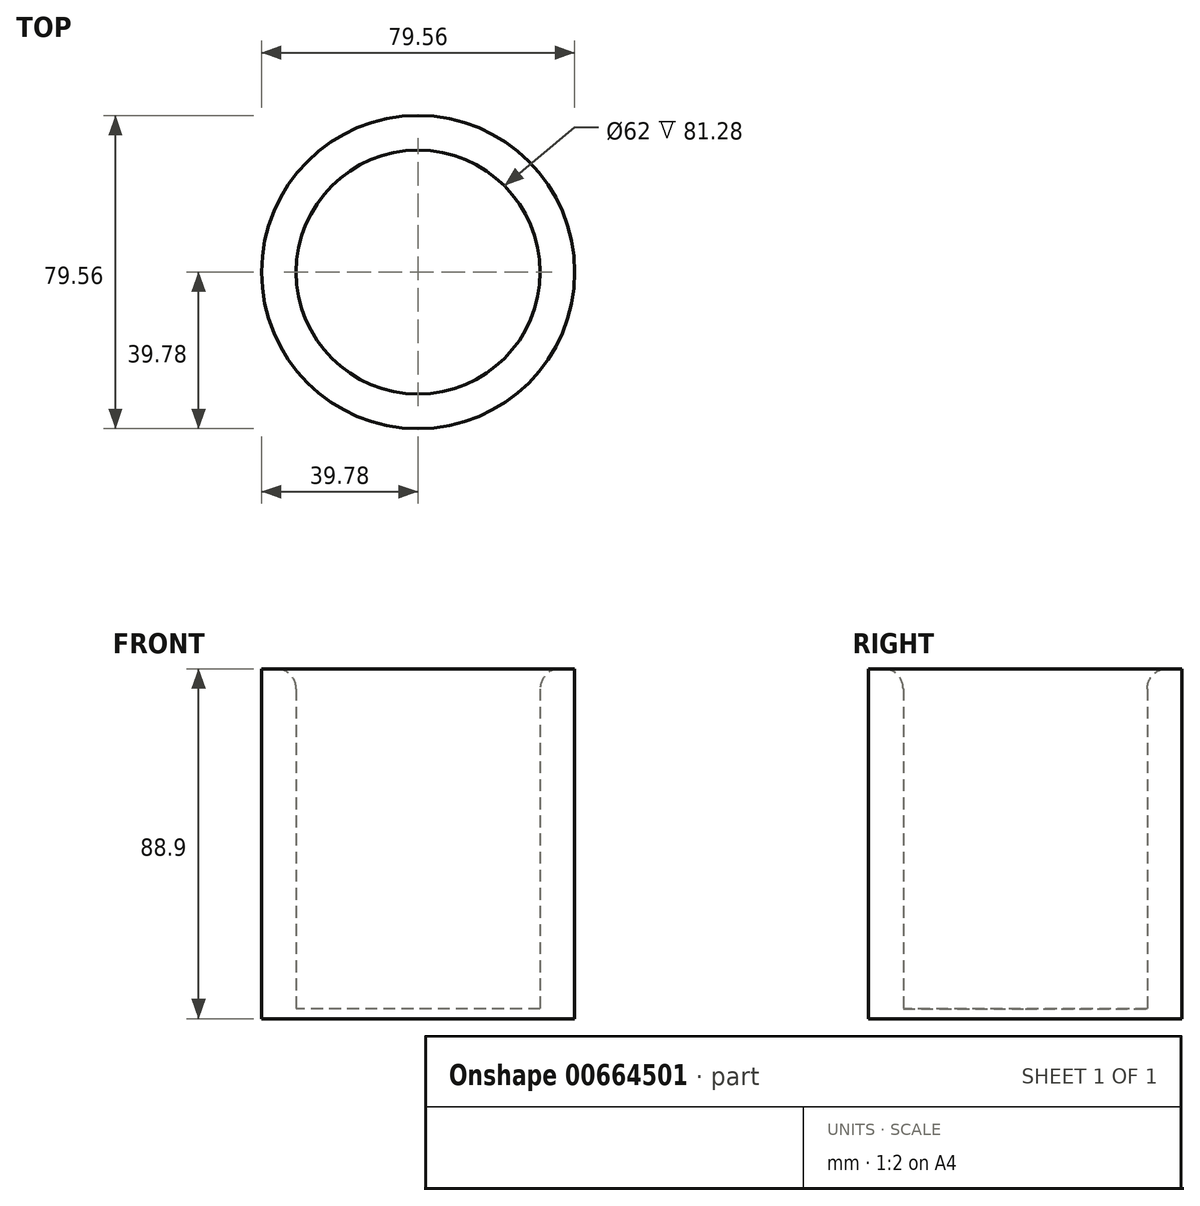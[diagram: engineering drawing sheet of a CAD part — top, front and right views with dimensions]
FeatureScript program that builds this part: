
annotation { "Feature Type Name" : "Feature", "Feature Type Description" : "" }
export const myFeature = defineFeature(function(context is Context, id is Id, definition is map)
    precondition{}
    {
        {
            var Q0;
            Q0=qCreatedBy(makeId("Top.planeOp"),FACE);
            var sketch = newSketch(context, id + "F0", { "sketchPlane" : qUnion([Q0])});
            skCircle(sketch, "E0", {"center": v(0, 0) * mm, "radius": 31 * mm});
            skCircle(sketch, "E1", {"center": v(0, 0) * mm, "radius": 39.78 * mm});
            skSolve(sketch);
        }
        {
            var Q0;
            Q0=makeQuery(id+"F0.imprint","IMPRINT",FACE,{"disambiguationData":[TD([[makeQuery(id+"F0.imprint","IMPRINT",EDGE,{"derivedFrom":sQuery(id+"F0.wireOp",EDGE,"E0")}),-1.0]])]});
            extrude(context, id + "F1", {"entities" : qUnion([Q0]), "depth" : 88.9 * mm, "offsetDistance" : 25.4 * mm});
        }
        {
            var Q0;
            Q0=makeQuery(id+"F0.imprint","IMPRINT",FACE,{"disambiguationData":[TD([[makeQuery(id+"F0.imprint","IMPRINT",EDGE,{"derivedFrom":sQuery(id+"F0.wireOp",EDGE,"E0")}),1.0]])]});
            extrude(context, id + "F2", {"entities" : qUnion([Q0]), "operationType" : NewBodyOperationType.ADD, "depth" : 2.54 * mm, "offsetDistance" : 25.4 * mm});
        }
        {
            var Q0;
            Q0=makeQuery(id+"F1.opExtrude","CAP_EDGE",EDGE,{"disambiguationData":[OSD([sQuery(id+"F0.wireOp",EDGE,"E0")])],"isStart":false});
            fillet(context, id + "F3", {"entities" : qUnion([Q0]), "radius" : 5.08 * mm, "tangentPropagation" : true, "allowEdgeOverflow" : false});
        }
    });
